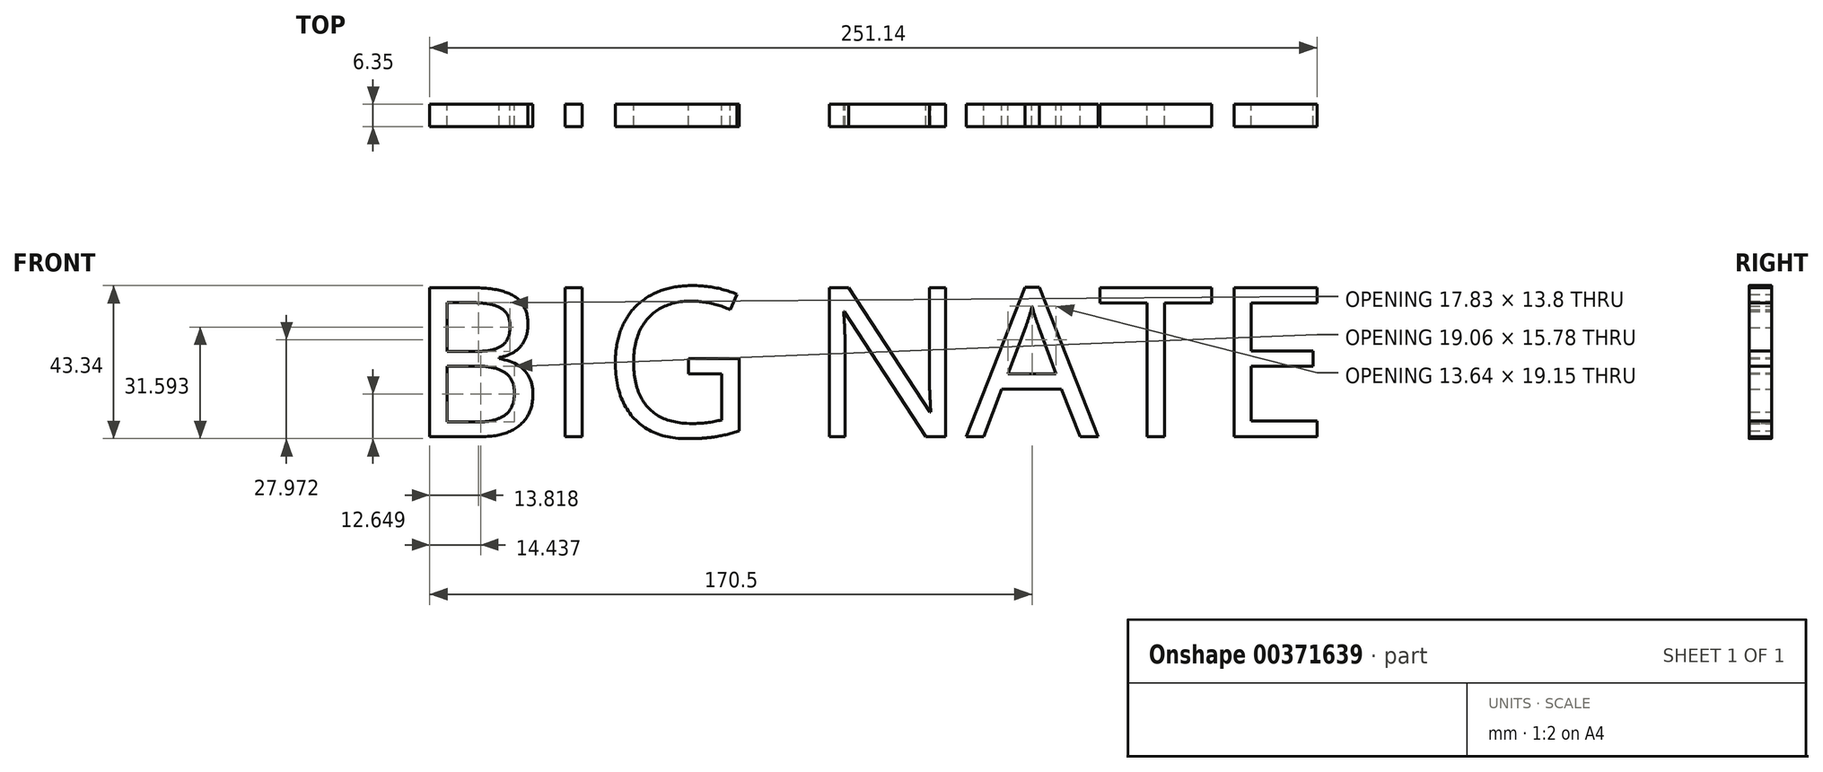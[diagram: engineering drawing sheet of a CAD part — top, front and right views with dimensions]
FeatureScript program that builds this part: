
annotation { "Feature Type Name" : "Feature", "Feature Type Description" : "" }
export const myFeature = defineFeature(function(context is Context, id is Id, definition is map)
    precondition{}
    {
        {
            var Q0;
            Q0=qCreatedBy(makeId("Front.planeOp"),FACE);
            var sketch = newSketch(context, id + "F0", { "sketchPlane" : qUnion([Q0])});
            skText(sketch, "E0", { "text": "BIG NATE", "fontName": "OpenSans-Regular.ttf"});
            const initialGuessF0  = {"E0": [-0.135, -0.0259, 1, 0, 0.04252]};
            skSetInitialGuess(sketch, initialGuessF0);
            skSolve(sketch);
        }
        {
            var Q0;
            Q0 = qSketchRegion(id + "F0", true);
            extrude(context, id + "F1", {"entities" : qUnion([Q0]), "depth" : 6.35 * mm});
        }
    });
